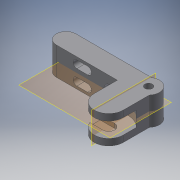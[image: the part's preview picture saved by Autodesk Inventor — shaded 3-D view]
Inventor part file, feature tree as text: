
AUTODESK INVENTOR PART (.ipt)
format: ipt  version: 2018 (Build 220112000, 112)  size: 234,496 bytes
history: native  units: mm
features: extrude x10, sketch x8, reference x6, other x3, plane x2, mirror x2, revolve x1
ambient origin geometry x8: Origin, YZ Plane, XZ Plane, XY Plane, X Axis, Y Axis, Z Axis, Center Point
bodies: Solid1 (feature_tree)
feature tree (32):
  extrude  "Extrusion1"  Depth=13.0mm
  extrude  "Extrusion6"  Depth=13.0mm
  extrude  "Extrusion7"  Depth=5.0mm
  plane  "Work Plane1"
  mirror  "Mirror3"
  extrude  "Extrusion2"  Depth=9.0mm
  plane  "Work Plane2"
  revolve  "Revolution1"  [1 undecoded]
  extrude  "Extrusion3"  Depth=1.0mm
  extrude  "Extrusion5"  Depth=3.5mm
  mirror  "Mirror4"
  extrude  "Extrusion8"  Depth=1.0mm TaperAngle=0.0deg
  sketch  "Sketch1"  dims[d0=13.0mm d1=0.0mm d2=0.2mm]
  reference  "Reference1"
  sketch  "Sketch2"  dims[d3=4.0mm d5=13.0mm]
  reference  "Reference2"
  reference  "Reference3"
  sketch  "Sketch4"  dims[d6=3.5mm d7=5.0mm]
  reference  "Reference6"
  reference  "Reference7"
  sketch  "Sketch5"  dims[d8=10.0mm d9=0.0mm d10=9.0mm]
  sketch  "Sketch7"  dims[d11=35.0mm d12=10.0mm]
  sketch  "Sketch8"  dims[d15=1.0mm d16=1.0mm]
  sketch  "Sketch9"  dims[d17=90.0deg d18=3.5mm]
  sketch  "Sketch10"  dims[d19=10.0mm d20=0.0mm d23=1.0mm d24=0.0mm d25=16.982573mm d26=1.0mm d27=0.0mm d28=1.0mm d29=0.0mm d30=5.0mm d31=3.0mm d32=10.0mm d33=0.0mm]
  reference  "Reference8"
  parser-record x1  (decoder bookkeeping rows leaked as tree rows — omitted from the tree; the rows remain in map.json)
  extrude  "Extruder Head.iam"  Depth=10.0mm
  other  "625 Bearing:1"
  extrude  "Extruder Body:1"  Depth=1.0mm TaperAngle=0.0deg
  other  "NEMA17:1"
  extrude  "Extruder:1"  Depth=1.0mm TaperAngle=0.0deg
note: 1 file-system path scrubbed to <path> (originals preserved in map.json)
note: 1 required parameter value undecoded (feature->parameter linkage not recoverable at this tier; creation-order binding heuristic only, values carry confidence <= 0.55)
